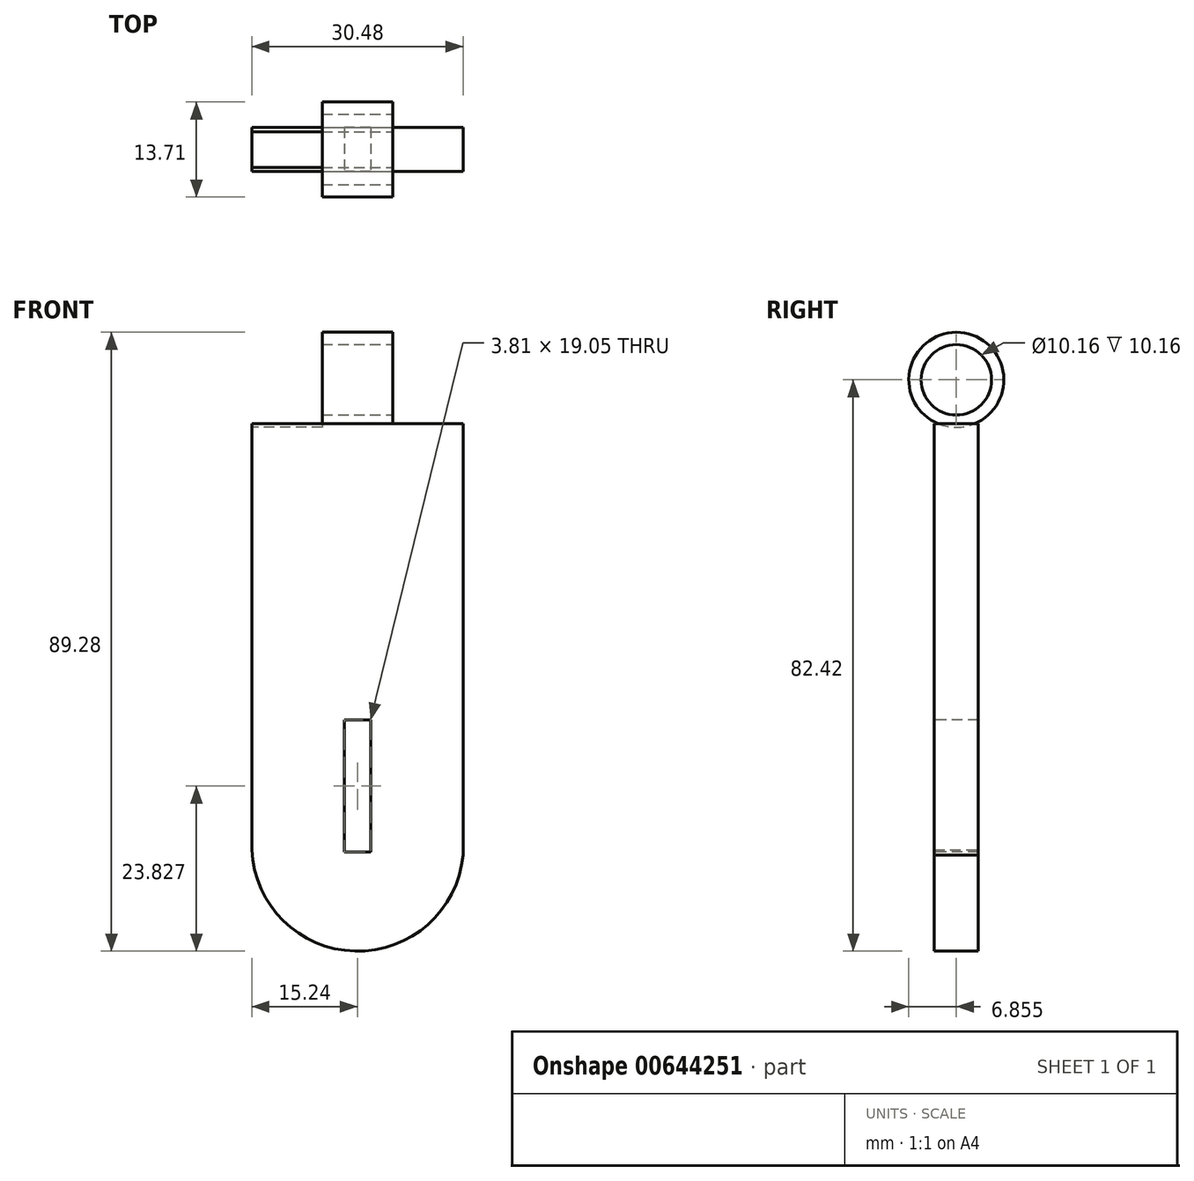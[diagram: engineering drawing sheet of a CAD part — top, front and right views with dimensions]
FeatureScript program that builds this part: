
annotation { "Feature Type Name" : "Feature", "Feature Type Description" : "" }
export const myFeature = defineFeature(function(context is Context, id is Id, definition is map)
    precondition{}
    {
        {
            var Q0;
            Q0=qCreatedBy(makeId("Front.planeOp"),FACE);
            var sketch = newSketch(context, id + "F0", { "sketchPlane" : qUnion([Q0])});
            skLineSegment(sketch, "E0.bottom", {"start": v(0, 0) * mm, "end": v(30.48, 0) * mm});
            skLineSegment(sketch, "E0.top", {"start": v(0, -76.2) * mm, "end": v(30.48, -76.2) * mm});
            skLineSegment(sketch, "E0.left", {"start": v(0, 0) * mm, "end": v(0, -76.2) * mm});
            skLineSegment(sketch, "E0.right", {"start": v(30.48, 0) * mm, "end": v(30.48, -76.2) * mm});
            skArc(sketch, "E1", {"start": v(0, -61.44) * mm, "mid": v(16.3, -76.03) * mm, "end": v(30.48, -59.36) * mm});
            skSolve(sketch);
        }
        {
            var Q0;
            {var subQ1=sQuery(id+"F0.wireOp",EDGE,"E0.bottom");Q0=makeQuery(id+"F0.imprint","IMPRINT",FACE,{"disambiguationData":[TD([[makeQuery(id+"F0.imprint","IMPRINT",EDGE,{"derivedFrom":subQ1}),-1.0]])]});}
            extrude(context, id + "F1", {"entities" : qUnion([Q0]), "depth" : 6.35 * mm, "offsetDistance" : 25.4 * mm});
        }
        {
            var Q0;
            Q0=makeQuery(id+"F1.opExtrude","SWEPT_FACE",FACE,{"disambiguationData":[OSD([sQuery(id+"F0.wireOp",EDGE,"E0.left")])]});
            var sketch = newSketch(context, id + "F2", { "sketchPlane" : qUnion([Q0])});
            skCircle(sketch, "E2", {"center": v(3.18, 6.35) * mm, "radius": 6.86 * mm});
            skPoint(sketch, "E2.centerSnap0", {"position": v(3.18, 0) * mm});
            skSolve(sketch);
        }
        {
            var Q0;
            Q0 = qSketchRegion(id + "F2", true);
            extrude(context, id + "F3", {"entities" : qUnion([Q0]), "operationType" : NewBodyOperationType.ADD, "depth" : 10.16 * mm, "offsetDistance" : 25.4 * mm, "hasSecondDirection" : true, "secondDirectionOppositeDirection" : true, "secondDirectionDepth" : 20.32 * mm});
        }
        {
            var Q0;
            Q0=makeQuery(id+"F3.boolean.opBoolean","MERGE",FACE,{"derivedFrom":[makeQuery(id+"F1.opExtrude","SWEPT_FACE",FACE,{"disambiguationData":[OSD([sQuery(id+"F0.wireOp",EDGE,"E0.right")])]}),makeQuery(id+"F3.opExtrude","CAP_FACE",FACE,{"disambiguationData":[OSD([sQuery(id+"F2.wireOp",EDGE,"E2")])],"isStart":false})]});
            var sketch = newSketch(context, id + "F4", { "sketchPlane" : qUnion([Q0])});
            skCircle(sketch, "E3", {"center": v(-3.18, 6.35) * mm, "radius": 5.08 * mm});
            skSolve(sketch);
        }
        {
            var Q0;
            Q0=makeQuery(id+"F4.imprint","IMPRINT",FACE,{"disambiguationData":[TD([[makeQuery(id+"F4.imprint","IMPRINT",EDGE,{"derivedFrom":sQuery(id+"F4.wireOp",EDGE,"E3")}),1.0]])]});
            extrude(context, id + "F5", {"entities" : qUnion([Q0]), "operationType" : NewBodyOperationType.REMOVE, "oppositeDirection" : true, "depth" : 30.48 * mm, "offsetDistance" : 25.4 * mm});
        }
        {
            var Q0;
            Q0=makeQuery(id+"F3.opExtrude","CAP_FACE",FACE,{"disambiguationData":[OSD([sQuery(id+"F2.wireOp",EDGE,"E2")])],"isStart":false});
            extrude(context, id + "F6", {"entities" : qUnion([Q0]), "operationType" : NewBodyOperationType.REMOVE, "oppositeDirection" : true, "depth" : 20.32 * mm, "offsetDistance" : 25.4 * mm});
        }
        {
            var Q0;
            Q0=makeQuery(id+"F1.opExtrude","CAP_FACE",FACE,{"disambiguationData":[OSD([sQuery(id+"F0.wireOp",EDGE,"E0.bottom"),sQuery(id+"F0.wireOp",EDGE,"E0.left"),sQuery(id+"F0.wireOp",EDGE,"E0.right"),sQuery(id+"F0.wireOp",EDGE,"E1")])],"isStart":false});
            var sketch = newSketch(context, id + "F7", { "sketchPlane" : qUnion([Q0])});
            skLineSegment(sketch, "E4.bottom", {"start": v(17.14, -42.72) * mm, "end": v(13.33, -42.72) * mm});
            skLineSegment(sketch, "E4.top", {"start": v(17.14, -61.77) * mm, "end": v(13.33, -61.77) * mm});
            skLineSegment(sketch, "E4.left", {"start": v(17.14, -42.72) * mm, "end": v(17.14, -61.77) * mm});
            skLineSegment(sketch, "E4.right", {"start": v(13.33, -42.72) * mm, "end": v(13.33, -61.77) * mm});
            skPoint(sketch, "E4.middle", {"position": v(15.24, -52.24) * mm});
            skPoint(sketch, "E4.middle.positionSnap0", {"position": v(15.24, 0) * mm});
            skPoint(sketch, "E4.centerSnap0", {"position": v(15.24, 0) * mm});
            skSolve(sketch);
        }
        {
            var Q0;
            Q0 = qSketchRegion(id + "F7", true);
            extrude(context, id + "F8", {"entities" : qUnion([Q0]), "operationType" : NewBodyOperationType.REMOVE, "oppositeDirection" : true, "depth" : 25.4 * mm, "offsetDistance" : 25.4 * mm});
        }
    });
